# Revit family: Andreu World_Plaza_BM1068
name_source: partatom
category: Mobiliario
revit_build: Autodesk Revit 2014 (Build: 20130722_2115(x64)
units: mm (PartAtom-declared; Revit-internal decimal feet)

## types (1)
- BM-1068 400x400 Polished aluminum base with round aluminum column
    70x70 Square aluminum column = No
    80x80 Square aluminum column = No
    80x80 Square wood column = No
    90x90 Square wood column = No
    Aluminum Column Material = Andreu World Polished Aluminum
    Base Material = Andreu World Polished Aluminum
    Base height = 20 mm  [stored 0.0656168 ft]
    D100 Round wood column = No
    D80 Round aluminum column = Sí
    D90 Round aluminum column = No
    D90 Round wood column = No
    Depth = 400 mm  [stored 1.31234 ft]
    Descripción = Table base with central column with square injected aluminum base.
    Fabricante = Andreu World
    Height = 720 mm  [stored 2.3622 ft]
    Modelo = Plaza
    Referencia = BM-1068
    Round aluminum Diameter = 90 mm  [stored 0.295276 ft]
    URL = http://www.andreuworld.com
    Width = 400 mm  [stored 1.31234 ft]
    Wood Column Material = Andreu World Beech V

note: [stored X ft] marks values corroborated as IEEE doubles in the binary element streams (Revit-internal decimal feet)

## geometry (parser evidence)
native form markers: Blend x4
no freeform markers — native parametric forms only
